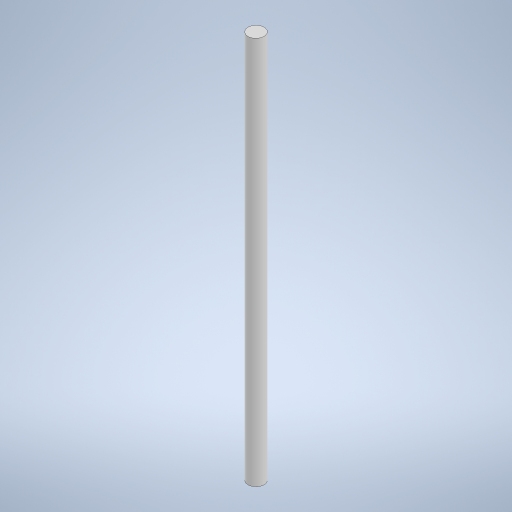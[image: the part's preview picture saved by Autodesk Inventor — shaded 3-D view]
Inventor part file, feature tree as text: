
AUTODESK INVENTOR PART (.ipt)
format: ipt  version: 2023 (Build 270158000, 158)  size: 228,864 bytes
history: native  units: in
note: dims shown in document units (in); Inventor stores cm internally (conversion verified against a paired STEP export)
features: extrude x1, sketch x1
ambient origin geometry x8: Origin, YZ Plane, XZ Plane, XY Plane, X Axis, Y Axis, Z Axis, Center Point
bodies: Solid1 (feature_tree)
feature tree (2):
  extrude  "Extrusion1"  Depth=3.0in TaperAngle=0.0deg
  sketch  "Sketch1"  dims[d0=0.125in d1=3.0in d2=0.0in]
